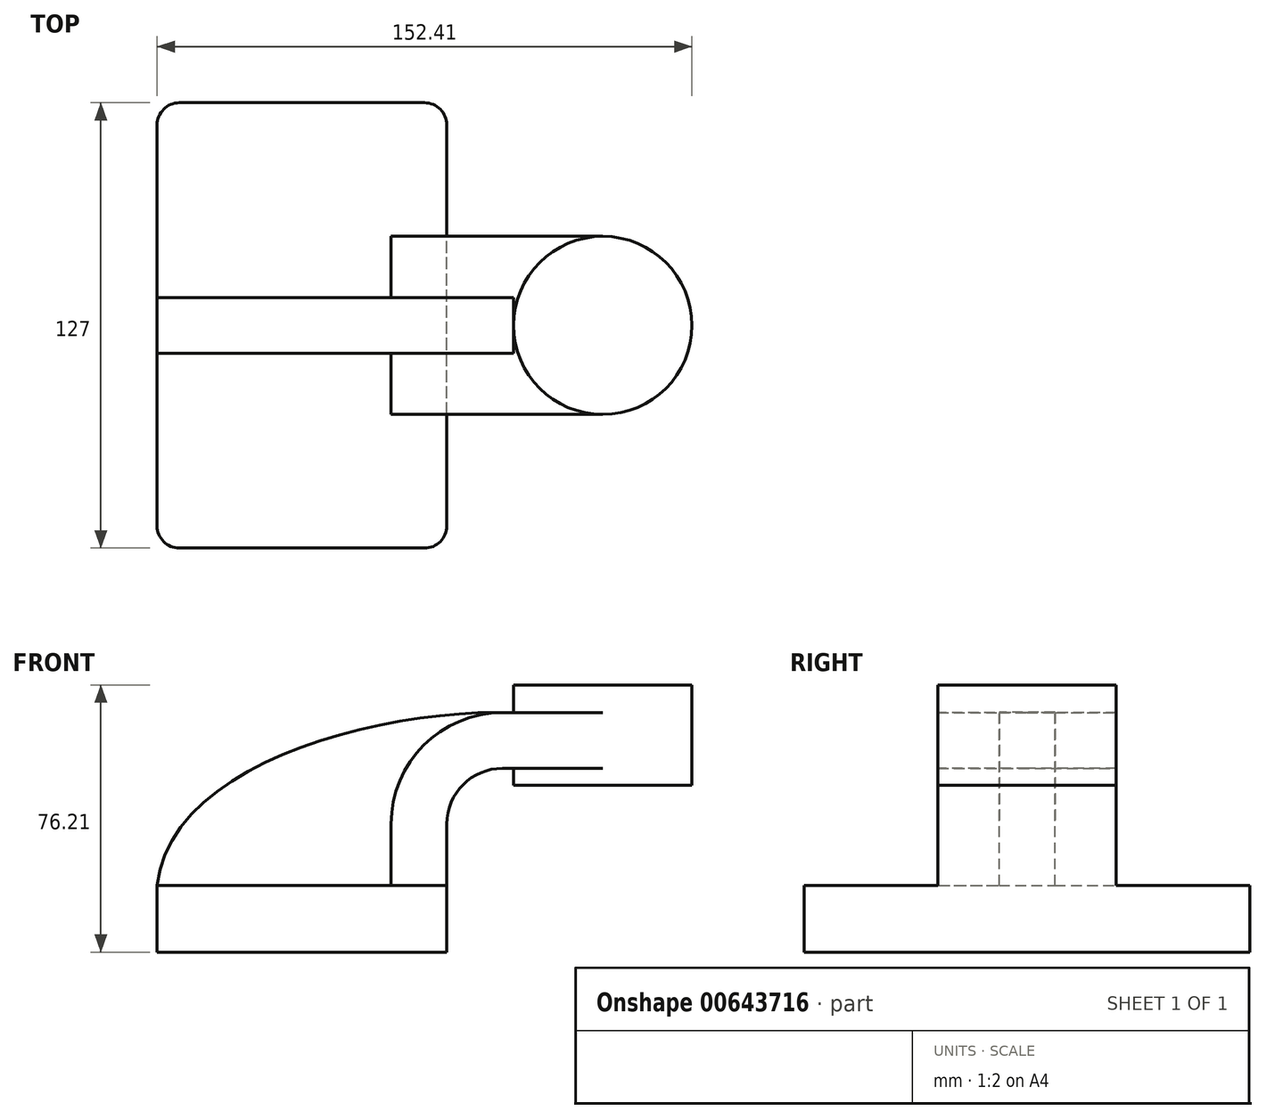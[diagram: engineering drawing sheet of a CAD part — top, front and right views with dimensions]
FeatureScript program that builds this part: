
annotation { "Feature Type Name" : "Feature", "Feature Type Description" : "" }
export const myFeature = defineFeature(function(context is Context, id is Id, definition is map)
    precondition{}
    {
        {
            var Q0;
            Q0=qCreatedBy(makeId("Front.planeOp"),FACE);
            var sketch = newSketch(context, id + "F0", { "sketchPlane" : qUnion([Q0])});
            skLineSegment(sketch, "E0.bottom", {"start": v(-41.28, -9.53) * mm, "end": v(41.28, -9.53) * mm});
            skLineSegment(sketch, "E0.top", {"start": v(-41.28, 9.52) * mm, "end": v(41.28, 9.52) * mm});
            skLineSegment(sketch, "E0.left", {"start": v(-41.27, -9.53) * mm, "end": v(-41.28, 9.52) * mm});
            skLineSegment(sketch, "E0.right", {"start": v(41.28, -9.53) * mm, "end": v(41.28, 9.52) * mm});
            skPoint(sketch, "E0.middle", {"position": v(0, 0) * mm});
            skLineSegment(sketch, "E1.bottom", {"start": v(60.32, 38.1) * mm, "end": v(111.12, 38.1) * mm});
            skLineSegment(sketch, "E1.top", {"start": v(60.32, 66.67) * mm, "end": v(111.12, 66.67) * mm});
            skLineSegment(sketch, "E1.left", {"start": v(60.32, 38.1) * mm, "end": v(60.32, 66.67) * mm});
            skLineSegment(sketch, "E1.right", {"start": v(111.12, 38.1) * mm, "end": v(111.12, 66.67) * mm});
            skPoint(sketch, "E1.middle", {"position": v(85.72, 52.39) * mm});
            skLineSegment(sketch, "E2", {"start": v(41.27, 9.52) * mm, "end": v(41.27, 27) * mm});
            skArc(sketch, "E3", {"start": v(41.27, 27) * mm, "mid": v(45.92, 38.23) * mm, "end": v(57.15, 42.88) * mm});
            skLineSegment(sketch, "E4", {"start": v(57.15, 42.88) * mm, "end": v(80.23, 42.88) * mm});
            skLineSegment(sketch, "E5.0", {"start": v(57.15, 58.75) * mm, "end": v(80.23, 58.75) * mm});
            skArc(sketch, "E5.1", {"start": v(25.4, 27) * mm, "mid": v(34.7, 49.45) * mm, "end": v(57.15, 58.75) * mm});
            skLineSegment(sketch, "E5.2", {"start": v(25.4, 9.52) * mm, "end": v(25.4, 27) * mm});
            skLineSegment(sketch, "E6", {"start": v(85.72, 38.1) * mm, "end": v(85.72, 66.67) * mm});
            skFitSpline(sketch, "E7", {"points": [v(-41.28, 9.52) * mm, v(60.32, 58.75) * mm], "startDerivative": vector(11.63, 106.17) * mm, "endDerivative": vector(111.06, -3.5) * mm});
            skLineSegment(sketch, "E8", {"start": v(25.4, 9.52) * mm, "end": v(41.28, 9.52) * mm});
            skLineSegment(sketch, "E9", {"start": v(80.23, 58.75) * mm, "end": v(85.72, 58.75) * mm});
            skLineSegment(sketch, "E10", {"start": v(80.23, 42.88) * mm, "end": v(85.72, 42.88) * mm});
            skSolve(sketch);
        }
        {
            var Q0;
            Q0=makeQuery(id+"F0.imprint","IMPRINT",FACE,{"disambiguationData":[TD([[makeQuery(id+"F0.imprint","IMPRINT",EDGE,{"derivedFrom":sQuery(id+"F0.wireOp",EDGE,"E0.bottom")}),1.0]])]});
            extrude(context, id + "F1", {"entities" : qUnion([Q0]), "endBound" : BoundingType.SYMMETRIC, "depth" : 127 * mm, "offsetDistance" : 25.4 * mm});
        }
        {
            var Q0;
            Q0=makeQuery(id+"F0.imprint","IMPRINT",FACE,{"disambiguationData":[TD([[makeQuery(id+"F0.imprint","IMPRINT",EDGE,{"derivedFrom":sQuery(id+"F0.wireOp",EDGE,"E0.top")}),1.0]])]});
            extrude(context, id + "F2", {"entities" : qUnion([Q0]), "operationType" : NewBodyOperationType.ADD, "endBound" : BoundingType.SYMMETRIC, "depth" : 15.88 * mm, "offsetDistance" : 25.4 * mm});
        }
        {
            var Q0;
            Q0=makeQuery(id+"F0.imprint","IMPRINT",FACE,{"disambiguationData":[TD([[makeQuery(id+"F0.imprint","IMPRINT",EDGE,{"derivedFrom":sQuery(id+"F0.wireOp",EDGE,"E2")}),1.0]])]});
            extrude(context, id + "F3", {"entities" : qUnion([Q0]), "operationType" : NewBodyOperationType.ADD, "endBound" : BoundingType.SYMMETRIC, "depth" : 50.8 * mm, "offsetDistance" : 25.4 * mm});
        }
        {
            var Q0;
            {var subQ0=sQuery(id+"F0.wireOp",EDGE,"E9");Q0=makeQuery(id+"F0.imprint","IMPRINT",FACE,{"disambiguationData":[TD([[makeQuery(id+"F0.imprint","IMPRINT",EDGE,{"derivedFrom":subQ0}),-1.0]])]});}
            extrude(context, id + "F4", {"entities" : qUnion([Q0]), "operationType" : NewBodyOperationType.ADD, "endBound" : BoundingType.SYMMETRIC, "depth" : 50.8 * mm, "offsetDistance" : 25.4 * mm});
        }
        {
            var Q0;
            {var subQ4=sQuery(id+"F0.wireOp",EDGE,"E1.right");Q0=makeQuery(id+"F0.imprint","IMPRINT",FACE,{"disambiguationData":[TD([[makeQuery(id+"F0.imprint","IMPRINT",EDGE,{"derivedFrom":subQ4}),1.0]])]});}
            var Q1;
            Q1=sQuery(id+"F0.wireOp",EDGE,"E6");
            revolve(context, id + "F5", {"operationType" : NewBodyOperationType.ADD, "entities" : qUnion([Q0]), "axis" : qUnion([Q1]), "revolveType" : RevolveType.FULL});
        }
        {
            var Q0;
            Q0=makeQuery(id+"F1.opExtrude","CAP_EDGE",EDGE,{"disambiguationData":[OSD([sQuery(id+"F0.wireOp",EDGE,"E0.right")])],"isStart":false});
            var Q1;
            Q1=makeQuery(id+"F1.opExtrude","CAP_EDGE",EDGE,{"disambiguationData":[OSD([sQuery(id+"F0.wireOp",EDGE,"E0.left")])],"isStart":false});
            var Q2;
            Q2=makeQuery(id+"F1.opExtrude","CAP_EDGE",EDGE,{"disambiguationData":[OSD([sQuery(id+"F0.wireOp",EDGE,"E0.right")])],"isStart":true});
            var Q3;
            Q3=makeQuery(id+"F1.opExtrude","CAP_EDGE",EDGE,{"disambiguationData":[OSD([sQuery(id+"F0.wireOp",EDGE,"E0.left")])],"isStart":true});
            fillet(context, id + "F6", {"entities" : qUnion([Q0, Q1, Q2, Q3]), "radius" : 6.35 * mm, "tangentPropagation" : true, "allowEdgeOverflow" : false});
        }
    });
